# Revit family: Accessory-Grab_Bar-KOHLER-K-33458T
name_source: partatom
category: Specialty Equipment
units: mm (PartAtom-declared; Revit-internal decimal feet)

## family parameters
Cut with Voids When Loaded = No
Host = Face
OmniClass Number = 23.31.25.00
OmniClass Title = Toilet and Bath Specialties
Part Type = Normal
Room Calculation Point = No
Round Connector Dimension = Use Diameter
Shared = No

## types (2) — shared parameters
ADA Compliant = No
Assembly Code = C1030200
Date Modified = 2/22/2024
Default Elevation = 42"
Description = 24 Inch Grab Bar
Height = 1 3/4"
Length = 26 3/4"
Manufacturer = Kohler Co.
Master Format 2014 = 10 28 00
Master Format 2014 Name = Toilet, Bath, and Laundry Accessories
Material = Premium Metal construction
URL = http://www.kohler.com.cn
WaterSense Certified = No
Width = 3 1/8"

## per-type parameters (varying)
| type | Finish | Model | Type |
| BL-Matte Black | Kohler-Metal-BL-Matte_Black | K-33458T-BL | 1 |
| CP-Polished Chrome | Kohler-Metal-CP-Polished_Chrome | K-33458T-CP | 2 |

## geometry (parser evidence)
native form markers: Sweep x5
no freeform markers — native parametric forms only
